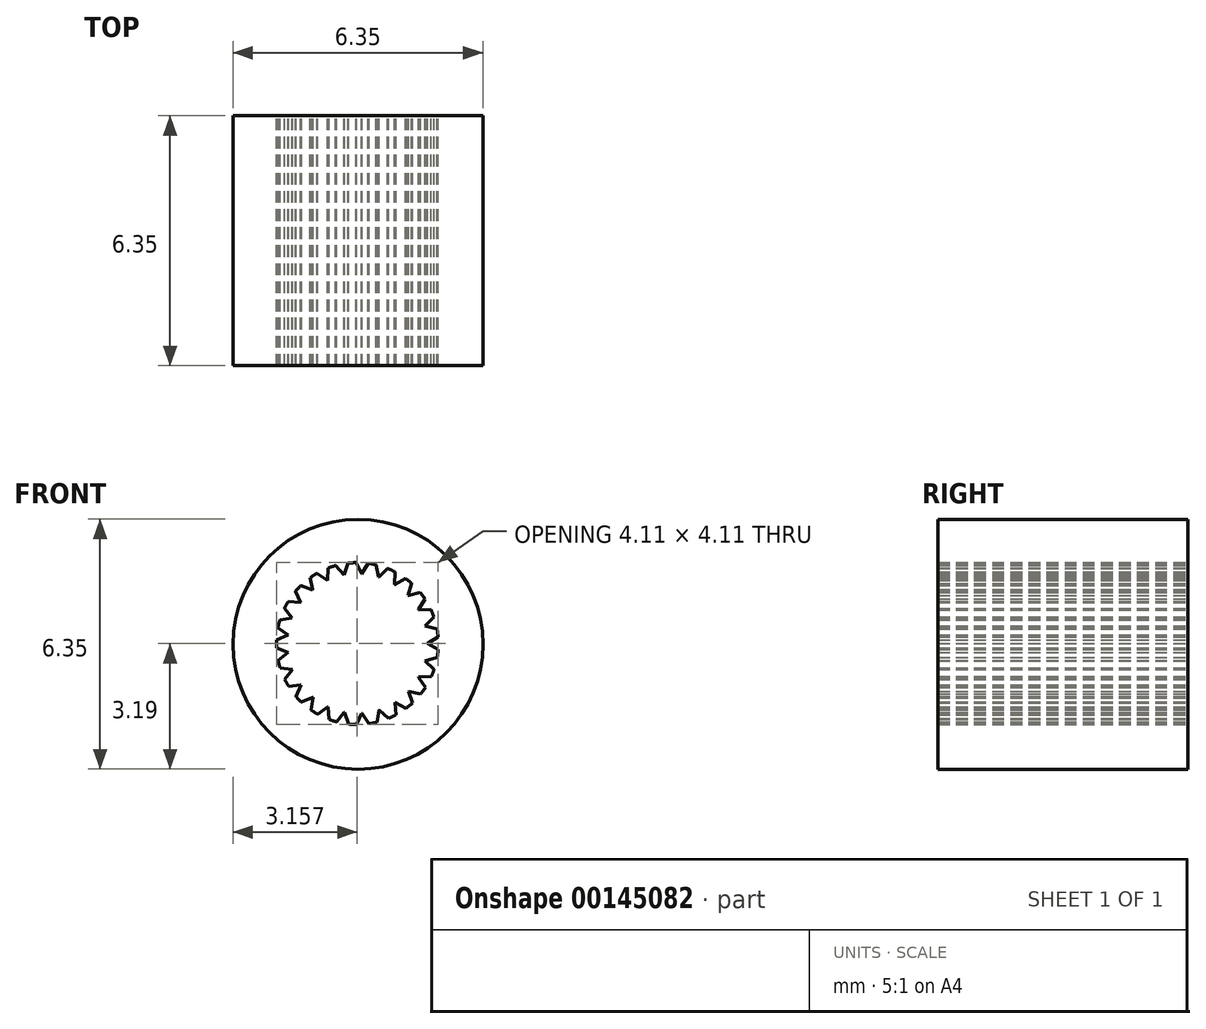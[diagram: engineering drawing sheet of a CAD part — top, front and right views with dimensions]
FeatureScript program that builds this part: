
annotation { "Feature Type Name" : "Feature", "Feature Type Description" : "" }
export const myFeature = defineFeature(function(context is Context, id is Id, definition is map)
    precondition{}
    {
        {
            var Q0;
            Q0=qCreatedBy(makeId("Front.planeOp"),FACE);
            var sketch = newSketch(context, id + "F0", { "sketchPlane" : qUnion([Q0])});
            skLineSegment(sketch, "E0", {"start": v(1.78, 0) * mm, "end": v(2.05, -0.15) * mm});
            skLineSegment(sketch, "E1.MirrorCS", {"start": v(1.72, -0.44) * mm, "end": v(2.03, -0.35) * mm});
            skArc(sketch, "E2", {"start": v(2.03, -0.35) * mm, "mid": v(2.04, -0.25) * mm, "end": v(2.05, -0.15) * mm});
            skPoint(sketch, "E3.center", {"position": v(0, 0) * mm});
            skArc(sketch, "E4.1.0", {"start": v(2.05, 0.17) * mm, "mid": v(2.04, 0.27) * mm, "end": v(2.02, 0.37) * mm});
            skLineSegment(sketch, "E4.1.1", {"start": v(1.78, 0) * mm, "end": v(2.05, 0.17) * mm});
            skLineSegment(sketch, "E4.1.2", {"start": v(1.72, 0.44) * mm, "end": v(2.02, 0.37) * mm});
            skArc(sketch, "E4.2.0", {"start": v(1.94, 0.67) * mm, "mid": v(1.9, 0.77) * mm, "end": v(1.87, 0.86) * mm});
            skLineSegment(sketch, "E4.2.1", {"start": v(1.72, 0.45) * mm, "end": v(1.94, 0.67) * mm});
            skLineSegment(sketch, "E4.2.2", {"start": v(1.56, 0.86) * mm, "end": v(1.87, 0.86) * mm});
            skArc(sketch, "E5.1.3.0", {"start": v(1.72, 1.13) * mm, "mid": v(1.66, 1.22) * mm, "end": v(1.6, 1.3) * mm});
            skLineSegment(sketch, "E5.4.3.0", {"start": v(1.55, 0.86) * mm, "end": v(1.72, 1.13) * mm});
            skLineSegment(sketch, "E5.7.3.0", {"start": v(1.3, 1.22) * mm, "end": v(1.6, 1.3) * mm});
            skArc(sketch, "E5.1.4.0", {"start": v(1.38, 1.53) * mm, "mid": v(1.3, 1.6) * mm, "end": v(1.22, 1.65) * mm});
            skLineSegment(sketch, "E5.4.4.0", {"start": v(1.3, 1.22) * mm, "end": v(1.38, 1.53) * mm});
            skLineSegment(sketch, "E5.7.4.0", {"start": v(0.95, 1.5) * mm, "end": v(1.22, 1.65) * mm});
            skArc(sketch, "E5.1.5.0", {"start": v(0.96, 1.82) * mm, "mid": v(0.87, 1.87) * mm, "end": v(0.77, 1.9) * mm});
            skLineSegment(sketch, "E5.4.5.0", {"start": v(0.95, 1.5) * mm, "end": v(0.96, 1.82) * mm});
            skLineSegment(sketch, "E5.7.5.0", {"start": v(0.55, 1.7) * mm, "end": v(0.77, 1.9) * mm});
            skArc(sketch, "E5.1.6.0", {"start": v(0.47, 2) * mm, "mid": v(0.37, 2.02) * mm, "end": v(0.27, 2.04) * mm});
            skLineSegment(sketch, "E5.4.6.0", {"start": v(0.54, 1.7) * mm, "end": v(0.47, 2) * mm});
            skLineSegment(sketch, "E5.7.6.0", {"start": v(0.11, 1.77) * mm, "end": v(0.27, 2.04) * mm});
            skArc(sketch, "E5.1.7.0", {"start": v(-0.04, 2.06) * mm, "mid": v(-0.14, 2.05) * mm, "end": v(-0.24, 2.04) * mm});
            skLineSegment(sketch, "E5.4.7.0", {"start": v(0.1, 1.78) * mm, "end": v(-0.04, 2.06) * mm});
            skLineSegment(sketch, "E5.7.7.0", {"start": v(-0.33, 1.75) * mm, "end": v(-0.24, 2.04) * mm});
            skArc(sketch, "E5.1.8.0", {"start": v(-0.55, 1.98) * mm, "mid": v(-0.65, 1.95) * mm, "end": v(-0.74, 1.92) * mm});
            skLineSegment(sketch, "E5.4.8.0", {"start": v(-0.34, 1.75) * mm, "end": v(-0.55, 1.98) * mm});
            skLineSegment(sketch, "E5.7.8.0", {"start": v(-0.76, 1.6) * mm, "end": v(-0.74, 1.92) * mm});
            skArc(sketch, "E5.1.9.0", {"start": v(-1.02, 1.78) * mm, "mid": v(-1.11, 1.73) * mm, "end": v(-1.2, 1.67) * mm});
            skLineSegment(sketch, "E5.4.9.0", {"start": v(-0.76, 1.6) * mm, "end": v(-1.02, 1.78) * mm});
            skLineSegment(sketch, "E5.7.9.0", {"start": v(-1.13, 1.37) * mm, "end": v(-1.2, 1.67) * mm});
            skArc(sketch, "E5.1.10.0", {"start": v(-1.44, 1.47) * mm, "mid": v(-1.5, 1.4) * mm, "end": v(-1.57, 1.32) * mm});
            skLineSegment(sketch, "E5.4.10.0", {"start": v(-1.14, 1.37) * mm, "end": v(-1.44, 1.47) * mm});
            skLineSegment(sketch, "E5.7.10.0", {"start": v(-1.44, 1.05) * mm, "end": v(-1.57, 1.32) * mm});
            skArc(sketch, "E5.1.11.0", {"start": v(-1.76, 1.07) * mm, "mid": v(-1.8, 0.98) * mm, "end": v(-1.85, 0.9) * mm});
            skLineSegment(sketch, "E5.4.11.0", {"start": v(-1.44, 1.04) * mm, "end": v(-1.76, 1.07) * mm});
            skLineSegment(sketch, "E5.7.11.0", {"start": v(-1.65, 0.65) * mm, "end": v(-1.85, 0.9) * mm});
            skArc(sketch, "E5.1.12.0", {"start": v(-1.97, 0.6) * mm, "mid": v(-2, 0.5) * mm, "end": v(-2.02, 0.4) * mm});
            skLineSegment(sketch, "E5.4.12.0", {"start": v(-1.66, 0.65) * mm, "end": v(-1.97, 0.6) * mm});
            skLineSegment(sketch, "E5.7.12.0", {"start": v(-1.76, 0.22) * mm, "end": v(-2.02, 0.4) * mm});
            skArc(sketch, "E5.1.13.0", {"start": v(-2.06, 0.1) * mm, "mid": v(-2.06, -0.01) * mm, "end": v(-2.05, -0.11) * mm});
            skLineSegment(sketch, "E5.4.13.0", {"start": v(-1.77, 0.22) * mm, "end": v(-2.06, 0.1) * mm});
            skLineSegment(sketch, "E5.7.13.0", {"start": v(-1.76, -0.22) * mm, "end": v(-2.05, -0.11) * mm});
            skArc(sketch, "E5.1.14.0", {"start": v(-2.01, -0.42) * mm, "mid": v(-1.99, -0.52) * mm, "end": v(-1.96, -0.62) * mm});
            skLineSegment(sketch, "E5.4.14.0", {"start": v(-1.76, -0.23) * mm, "end": v(-2.01, -0.42) * mm});
            skLineSegment(sketch, "E5.7.14.0", {"start": v(-1.65, -0.65) * mm, "end": v(-1.96, -0.62) * mm});
            skArc(sketch, "E5.1.15.0", {"start": v(-1.84, -0.91) * mm, "mid": v(-1.8, -1) * mm, "end": v(-1.75, -1.09) * mm});
            skLineSegment(sketch, "E5.4.15.0", {"start": v(-1.65, -0.66) * mm, "end": v(-1.84, -0.91) * mm});
            skLineSegment(sketch, "E5.7.15.0", {"start": v(-1.44, -1.05) * mm, "end": v(-1.75, -1.09) * mm});
            skArc(sketch, "E5.1.16.0", {"start": v(-1.56, -1.34) * mm, "mid": v(-1.5, -1.42) * mm, "end": v(-1.42, -1.49) * mm});
            skLineSegment(sketch, "E5.4.16.0", {"start": v(-1.43, -1.05) * mm, "end": v(-1.56, -1.34) * mm});
            skLineSegment(sketch, "E5.7.16.0", {"start": v(-1.13, -1.37) * mm, "end": v(-1.42, -1.49) * mm});
            skArc(sketch, "E5.1.17.0", {"start": v(-1.18, -1.69) * mm, "mid": v(-1.1, -1.74) * mm, "end": v(-1, -1.8) * mm});
            skLineSegment(sketch, "E5.4.17.0", {"start": v(-1.13, -1.37) * mm, "end": v(-1.18, -1.69) * mm});
            skLineSegment(sketch, "E5.7.17.0", {"start": v(-0.76, -1.6) * mm, "end": v(-1, -1.8) * mm});
            skArc(sketch, "E5.1.18.0", {"start": v(-0.72, -1.93) * mm, "mid": v(-0.63, -1.96) * mm, "end": v(-0.53, -1.99) * mm});
            skLineSegment(sketch, "E5.4.18.0", {"start": v(-0.75, -1.61) * mm, "end": v(-0.72, -1.93) * mm});
            skLineSegment(sketch, "E5.7.18.0", {"start": v(-0.33, -1.75) * mm, "end": v(-0.53, -1.99) * mm});
            skArc(sketch, "E5.1.19.0", {"start": v(-0.22, -2.05) * mm, "mid": v(-0.12, -2.05) * mm, "end": v(-0.02, -2.06) * mm});
            skLineSegment(sketch, "E5.4.19.0", {"start": v(-0.33, -1.75) * mm, "end": v(-0.22, -2.05) * mm});
            skLineSegment(sketch, "E5.7.19.0", {"start": v(0.11, -1.77) * mm, "end": v(-0.02, -2.06) * mm});
            skArc(sketch, "E5.1.20.0", {"start": v(0.3, -2.04) * mm, "mid": v(0.4, -2.02) * mm, "end": v(0.5, -2) * mm});
            skLineSegment(sketch, "E5.4.20.0", {"start": v(0.12, -1.77) * mm, "end": v(0.3, -2.04) * mm});
            skLineSegment(sketch, "E5.7.20.0", {"start": v(0.55, -1.7) * mm, "end": v(0.5, -2) * mm});
            skArc(sketch, "E5.1.21.0", {"start": v(0.8, -1.9) * mm, "mid": v(0.89, -1.86) * mm, "end": v(0.98, -1.81) * mm});
            skLineSegment(sketch, "E5.4.21.0", {"start": v(0.56, -1.69) * mm, "end": v(0.8, -1.9) * mm});
            skLineSegment(sketch, "E5.7.21.0", {"start": v(0.95, -1.5) * mm, "end": v(0.98, -1.81) * mm});
            skArc(sketch, "E5.1.22.0", {"start": v(1.24, -1.64) * mm, "mid": v(1.32, -1.58) * mm, "end": v(1.4, -1.51) * mm});
            skLineSegment(sketch, "E5.4.22.0", {"start": v(0.96, -1.5) * mm, "end": v(1.24, -1.64) * mm});
            skLineSegment(sketch, "E5.7.22.0", {"start": v(1.3, -1.22) * mm, "end": v(1.4, -1.51) * mm});
            skArc(sketch, "E5.1.23.0", {"start": v(1.6, -1.28) * mm, "mid": v(1.67, -1.2) * mm, "end": v(1.73, -1.12) * mm});
            skLineSegment(sketch, "E5.4.23.0", {"start": v(1.3, -1.21) * mm, "end": v(1.6, -1.28) * mm});
            skLineSegment(sketch, "E5.7.23.0", {"start": v(1.56, -0.86) * mm, "end": v(1.73, -1.12) * mm});
            skArc(sketch, "E5.1.24.0", {"start": v(1.88, -0.84) * mm, "mid": v(1.92, -0.75) * mm, "end": v(1.95, -0.65) * mm});
            skLineSegment(sketch, "E5.4.24.0", {"start": v(1.56, -0.85) * mm, "end": v(1.88, -0.84) * mm});
            skLineSegment(sketch, "E5.7.24.0", {"start": v(1.72, -0.44) * mm, "end": v(1.95, -0.65) * mm});
            skArc(sketch, "E6", {"start": v(1.78, 0) * mm, "mid": v(1.78, 0) * mm, "end": v(1.78, 0) * mm});
            skArc(sketch, "E7.trimOffspring", {"start": v(1.72, -0.44) * mm, "mid": v(1.72, -0.44) * mm, "end": v(1.72, -0.44) * mm});
            skArc(sketch, "E8.trimOffspring", {"start": v(1.56, -0.86) * mm, "mid": v(1.56, -0.85) * mm, "end": v(1.56, -0.85) * mm});
            skArc(sketch, "E9.trimOffspring", {"start": v(1.3, -1.22) * mm, "mid": v(1.3, -1.21) * mm, "end": v(1.3, -1.21) * mm});
            skArc(sketch, "E10.trimOffspring", {"start": v(0.95, -1.5) * mm, "mid": v(0.96, -1.5) * mm, "end": v(0.96, -1.5) * mm});
            skArc(sketch, "E11.trimOffspring", {"start": v(0.55, -1.7) * mm, "mid": v(0.55, -1.7) * mm, "end": v(0.56, -1.69) * mm});
            skArc(sketch, "E12.trimOffspring", {"start": v(0.11, -1.77) * mm, "mid": v(0.12, -1.77) * mm, "end": v(0.12, -1.77) * mm});
            skArc(sketch, "E13.trimOffspring", {"start": v(-0.33, -1.75) * mm, "mid": v(-0.33, -1.75) * mm, "end": v(-0.33, -1.75) * mm});
            skArc(sketch, "E14.trimOffspring", {"start": v(-0.76, -1.6) * mm, "mid": v(-0.75, -1.61) * mm, "end": v(-0.75, -1.61) * mm});
            skArc(sketch, "E15.trimOffspring", {"start": v(-1.44, -1.05) * mm, "mid": v(-1.44, -1.05) * mm, "end": v(-1.43, -1.05) * mm});
            skArc(sketch, "E16.trimOffspring", {"start": v(-1.65, -0.65) * mm, "mid": v(-1.65, -0.66) * mm, "end": v(-1.65, -0.66) * mm});
            skArc(sketch, "E17.trimOffspring", {"start": v(-1.13, -1.37) * mm, "mid": v(-1.13, -1.37) * mm, "end": v(-1.13, -1.37) * mm});
            skArc(sketch, "E18.trimOffspring", {"start": v(-1.76, -0.22) * mm, "mid": v(-1.76, -0.23) * mm, "end": v(-1.76, -0.23) * mm});
            skArc(sketch, "E19.trimOffspring", {"start": v(-1.76, 0.22) * mm, "mid": v(-1.76, 0.22) * mm, "end": v(-1.77, 0.22) * mm});
            skArc(sketch, "E20.trimOffspring", {"start": v(-1.65, 0.65) * mm, "mid": v(-1.65, 0.65) * mm, "end": v(-1.66, 0.65) * mm});
            skArc(sketch, "E21.trimOffspring", {"start": v(-1.44, 1.05) * mm, "mid": v(-1.44, 1.04) * mm, "end": v(-1.44, 1.04) * mm});
            skArc(sketch, "E22.trimOffspring", {"start": v(-1.13, 1.37) * mm, "mid": v(-1.14, 1.37) * mm, "end": v(-1.14, 1.37) * mm});
            skArc(sketch, "E23.trimOffspring", {"start": v(-0.76, 1.6) * mm, "mid": v(-0.76, 1.6) * mm, "end": v(-0.76, 1.6) * mm});
            skArc(sketch, "E24.trimOffspring", {"start": v(-0.33, 1.75) * mm, "mid": v(-0.34, 1.75) * mm, "end": v(-0.34, 1.75) * mm});
            skArc(sketch, "E25.trimOffspring", {"start": v(0.11, 1.77) * mm, "mid": v(0.1, 1.78) * mm, "end": v(0.1, 1.78) * mm});
            skArc(sketch, "E26.trimOffspring", {"start": v(0.55, 1.7) * mm, "mid": v(0.55, 1.7) * mm, "end": v(0.54, 1.7) * mm});
            skArc(sketch, "E27.trimOffspring", {"start": v(0.95, 1.5) * mm, "mid": v(0.95, 1.5) * mm, "end": v(0.95, 1.5) * mm});
            skArc(sketch, "E28.trimOffspring", {"start": v(1.3, 1.22) * mm, "mid": v(1.3, 1.22) * mm, "end": v(1.3, 1.22) * mm});
            skArc(sketch, "E29.trimOffspring", {"start": v(1.56, 0.86) * mm, "mid": v(1.56, 0.86) * mm, "end": v(1.55, 0.86) * mm});
            skArc(sketch, "E30.trimOffspring", {"start": v(1.72, 0.44) * mm, "mid": v(1.72, 0.45) * mm, "end": v(1.72, 0.45) * mm});
            skCircle(sketch, "E31", {"center": v(0.02, -0.02) * mm, "radius": 3.18 * mm});
            skSolve(sketch);
        }
        {
            var Q0;
            Q0=makeQuery(id+"F0.imprint","IMPRINT",FACE,{"disambiguationData":[TD([[makeQuery(id+"F0.imprint","IMPRINT",EDGE,{"derivedFrom":sQuery(id+"F0.wireOp",EDGE,"E0")}),1.0]])]});
            extrude(context, id + "F1", {"entities" : qUnion([Q0]), "depth" : 6.35 * mm});
        }
    });
